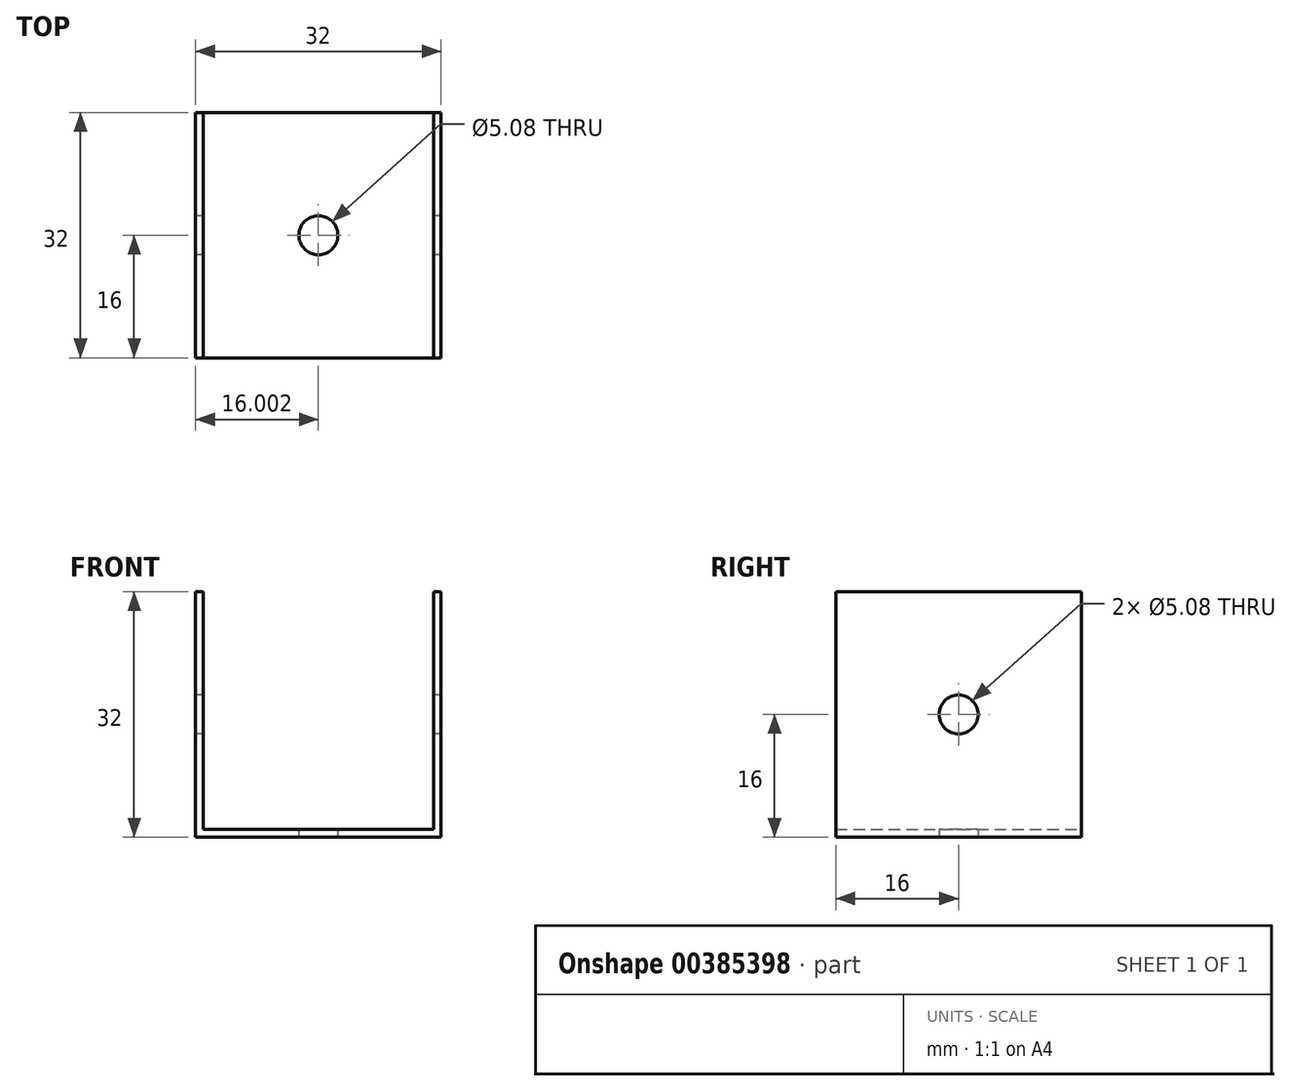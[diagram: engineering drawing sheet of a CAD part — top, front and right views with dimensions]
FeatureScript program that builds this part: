
annotation { "Feature Type Name" : "Feature", "Feature Type Description" : "" }
export const myFeature = defineFeature(function(context is Context, id is Id, definition is map)
    precondition{}
    {
        {
            var Q0;
            Q0=qCreatedBy(makeId("Front.planeOp"),FACE);
            var sketch = newSketch(context, id + "F0", { "sketchPlane" : qUnion([Q0])});
            skLineSegment(sketch, "E0", {"start": v(-19.82, 16.14) * mm, "end": v(-19.82, -15.86) * mm});
            skLineSegment(sketch, "E1", {"start": v(-19.82, -15.86) * mm, "end": v(12.18, -15.86) * mm});
            skLineSegment(sketch, "E2", {"start": v(12.18, -15.86) * mm, "end": v(12.18, 16.14) * mm});
            skLineSegment(sketch, "E3", {"start": v(12.18, 16.14) * mm, "end": v(11.18, 16.14) * mm});
            skLineSegment(sketch, "E4", {"start": v(11.18, 16.14) * mm, "end": v(11.18, -14.86) * mm});
            skLineSegment(sketch, "E5", {"start": v(11.18, -14.86) * mm, "end": v(-18.82, -14.86) * mm});
            skLineSegment(sketch, "E6", {"start": v(-18.82, -14.86) * mm, "end": v(-18.82, 16.14) * mm});
            skLineSegment(sketch, "E7", {"start": v(-18.82, 16.14) * mm, "end": v(-19.82, 16.14) * mm});
            skSolve(sketch);
        }
        {
            var Q0;
            Q0=qSketchRegion(id+"F0",true);
            extrude(context, id + "F1", {"entities" : qUnion([Q0]), "depth" : 32 * mm});
        }
        {
            var Q0;
            Q0=makeQuery(id+"F1.opExtrude","SWEPT_FACE",FACE,{"disambiguationData":[OSD([sQuery(id+"F0.wireOp",EDGE,"E0")])]});
            var sketch = newSketch(context, id + "F2", { "sketchPlane" : qUnion([Q0])});
            skPoint(sketch, "E8", {"position": v(16, 0.14) * mm});
            skCircle(sketch, "E9", {"center": v(16, 0.14) * mm, "radius": 2.54 * mm});
            skSolve(sketch);
        }
        {
            var Q0;
            Q0=makeQuery(id+"F2.imprint","IMPRINT",FACE,{"disambiguationData":[TD([[makeQuery(id+"F2.imprint","IMPRINT",EDGE,{"derivedFrom":sQuery(id+"F2.wireOp",EDGE,"E9")}),1.0]])]});
            extrude(context, id + "F3", {"entities" : qUnion([Q0]), "operationType" : NewBodyOperationType.REMOVE, "oppositeDirection" : true, "depth" : 76.2 * mm});
        }
        {
            var Q0;
            Q0=makeQuery(id+"F1.opExtrude","SWEPT_FACE",FACE,{"disambiguationData":[OSD([sQuery(id+"F0.wireOp",EDGE,"E1")])]});
            var sketch = newSketch(context, id + "F4", { "sketchPlane" : qUnion([Q0])});
            skPoint(sketch, "E10", {"position": v(-3.82, 16) * mm});
            skCircle(sketch, "E11", {"center": v(-3.82, 16) * mm, "radius": 2.54 * mm});
            skSolve(sketch);
        }
        {
            var Q0;
            Q0=makeQuery(id+"F4.imprint","IMPRINT",FACE,{"disambiguationData":[TD([[makeQuery(id+"F4.imprint","IMPRINT",EDGE,{"derivedFrom":sQuery(id+"F4.wireOp",EDGE,"E11")}),1.0]])]});
            extrude(context, id + "F5", {"entities" : qUnion([Q0]), "operationType" : NewBodyOperationType.REMOVE, "oppositeDirection" : true, "depth" : 25.4 * mm});
        }
    });
